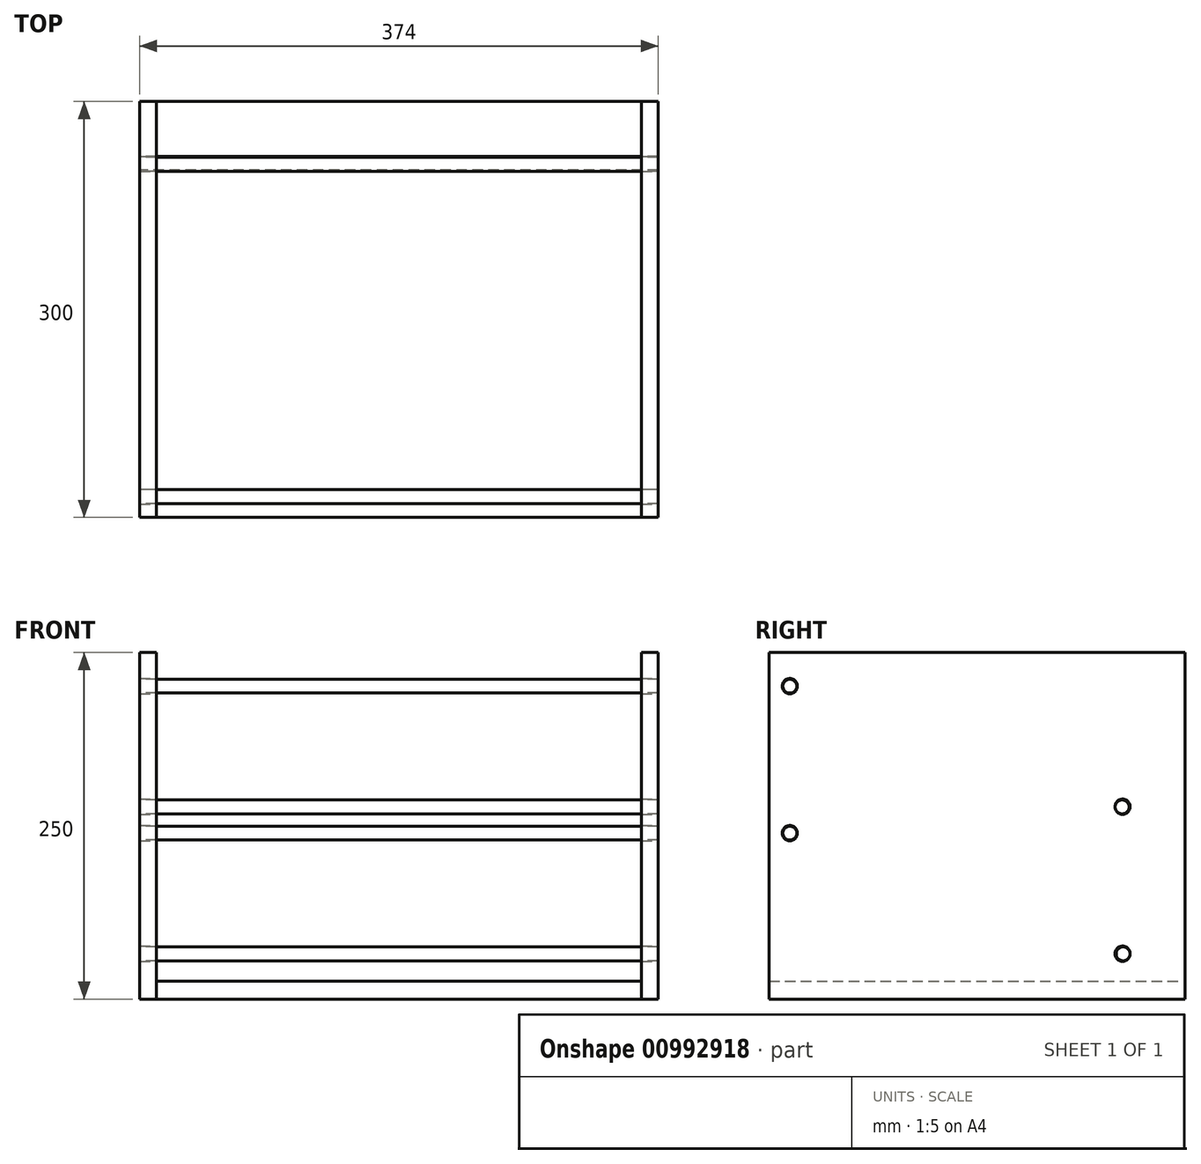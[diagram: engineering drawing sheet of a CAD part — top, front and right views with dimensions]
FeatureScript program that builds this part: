
annotation { "Feature Type Name" : "Feature", "Feature Type Description" : "" }
export const myFeature = defineFeature(function(context is Context, id is Id, definition is map)
    precondition{}
    {
        {
            var Q0;
            Q0=qCreatedBy(makeId("Top.planeOp"),FACE);
            var sketch = newSketch(context, id + "F0", { "sketchPlane" : qUnion([Q0])});
            skLineSegment(sketch, "E0.bottom", {"start": v(175, -150) * mm, "end": v(-175, -150) * mm});
            skLineSegment(sketch, "E0.top", {"start": v(175, 150) * mm, "end": v(-175, 150) * mm});
            skLineSegment(sketch, "E0.left", {"start": v(175, -150) * mm, "end": v(175, 150) * mm});
            skLineSegment(sketch, "E0.right", {"start": v(-175, -150) * mm, "end": v(-175, 150) * mm});
            skPoint(sketch, "E0.middle", {"position": v(0, 0) * mm});
            skSolve(sketch);
        }
        {
            var Q0;
            Q0 = qSketchRegion(id + "F0", true);
            extrude(context, id + "F1", {"entities" : qUnion([Q0]), "oppositeDirection" : true, "depth" : 13 * mm, "offsetDistance" : 25 * mm});
        }
        {
            var Q0;
            Q0=makeQuery(id+"F1.opExtrude","SWEPT_FACE",FACE,{"disambiguationData":[OSD([sQuery(id+"F0.wireOp",EDGE,"E0.left")])]});
            var sketch = newSketch(context, id + "F2", { "sketchPlane" : qUnion([Q0])});
            skLineSegment(sketch, "E1.bottom", {"start": v(-150, -13) * mm, "end": v(150, -13) * mm});
            skLineSegment(sketch, "E1.top", {"start": v(-150, 237) * mm, "end": v(150, 237) * mm});
            skLineSegment(sketch, "E1.left", {"start": v(-150, -13) * mm, "end": v(-150, 237) * mm});
            skLineSegment(sketch, "E1.right", {"start": v(150, -13) * mm, "end": v(150, 237) * mm});
            skSolve(sketch);
        }
        {
            var Q0;
            Q0 = qSketchRegion(id + "F2", true);
            extrude(context, id + "F3", {"entities" : qUnion([Q0]), "depth" : 12 * mm, "offsetDistance" : 25 * mm});
        }
        {
            var Q0;
            Q0=makeQuery(id+"F3.opExtrude","CAP_FACE",FACE,{"disambiguationData":[OSD([sQuery(id+"F2.wireOp",EDGE,"E1.bottom"),sQuery(id+"F2.wireOp",EDGE,"E1.top"),sQuery(id+"F2.wireOp",EDGE,"E1.left"),sQuery(id+"F2.wireOp",EDGE,"E1.right")])],"isStart":false});
            var sketch = newSketch(context, id + "F4", { "sketchPlane" : qUnion([Q0])});
            skCircle(sketch, "E2", {"center": v(-135, 106.7) * mm, "radius": 5.5 * mm});
            skCircle(sketch, "E3", {"center": v(-135, 212.7) * mm, "radius": 5.5 * mm});
            skCircle(sketch, "E4", {"center": v(105, 125.7) * mm, "radius": 5.5 * mm});
            skCircle(sketch, "E5", {"center": v(105, 19.7) * mm, "radius": 5.5 * mm});
            skSolve(sketch);
        }
        {
            var Q0;
            Q0 = qSketchRegion(id + "F4", true);
            extrude(context, id + "F5", {"entities" : qUnion([Q0]), "operationType" : NewBodyOperationType.REMOVE, "endBound" : BoundingType.THROUGH_ALL, "oppositeDirection" : true, "depth" : 25 * mm, "offsetDistance" : 25 * mm});
        }
        {
            var Q0;
            Q0=makeQuery(id+"F3.opExtrude","SWEPT_BODY",BODY,{"disambiguationData":[OSD([sQuery(id+"F2.wireOp",EDGE,"E1.bottom"),sQuery(id+"F2.wireOp",EDGE,"E1.top"),sQuery(id+"F2.wireOp",EDGE,"E1.left"),sQuery(id+"F2.wireOp",EDGE,"E1.right")])]});
            transform(context, id + "F6", {"entities" : qUnion([Q0]), "transformType" : TransformType.TRANSLATION_3D, "dx" : -362 * mm, "dy" : 0 * mm, "dz" : 0 * mm, "makeCopy" : true});
        }
        {
            var Q0;
            Q0=qCreatedBy(makeId("Right.planeOp"),FACE);
            var sketch = newSketch(context, id + "F7", { "sketchPlane" : qUnion([Q0])});
            skCircle(sketch, "E6", {"center": v(-135, 212.7) * mm, "radius": 5 * mm});
            skSolve(sketch);
        }
        {
            var Q0;
            Q0 = qSketchRegion(id + "F7", true);
            extrude(context, id + "F8", {"entities" : qUnion([Q0]), "endBound" : BoundingType.SYMMETRIC, "depth" : 374 * mm, "offsetDistance" : 25 * mm});
        }
        {
            var Q0;
            Q0=makeQuery(id+"F8.opExtrude","SWEPT_BODY",BODY,{"disambiguationData":[OSD([sQuery(id+"F7.wireOp",EDGE,"E6")])]});
            transform(context, id + "F9", {"entities" : qUnion([Q0]), "transformType" : TransformType.TRANSLATION_3D, "dx" : 0 * mm, "dy" : 0 * mm, "dz" : -106 * mm, "makeCopy" : true});
        }
        {
            var Q0;
            Q0=makeQuery(id+"F8.opExtrude","SWEPT_BODY",BODY,{"disambiguationData":[OSD([sQuery(id+"F7.wireOp",EDGE,"E6")])]});
            transform(context, id + "F10", {"entities" : qUnion([Q0]), "transformType" : TransformType.TRANSLATION_3D, "dx" : 0 * mm, "dy" : 239.7 * mm, "dz" : -87.1 * mm, "makeCopy" : true});
        }
        {
            var Q0;
            Q0=makeQuery(id+"F8.opExtrude","SWEPT_BODY",BODY,{"disambiguationData":[OSD([sQuery(id+"F7.wireOp",EDGE,"E6")])]});
            transform(context, id + "F11", {"entities" : qUnion([Q0]), "transformType" : TransformType.TRANSLATION_3D, "dx" : 0 * mm, "dy" : 240.4 * mm, "dz" : -193.1 * mm, "makeCopy" : true});
        }
    });
